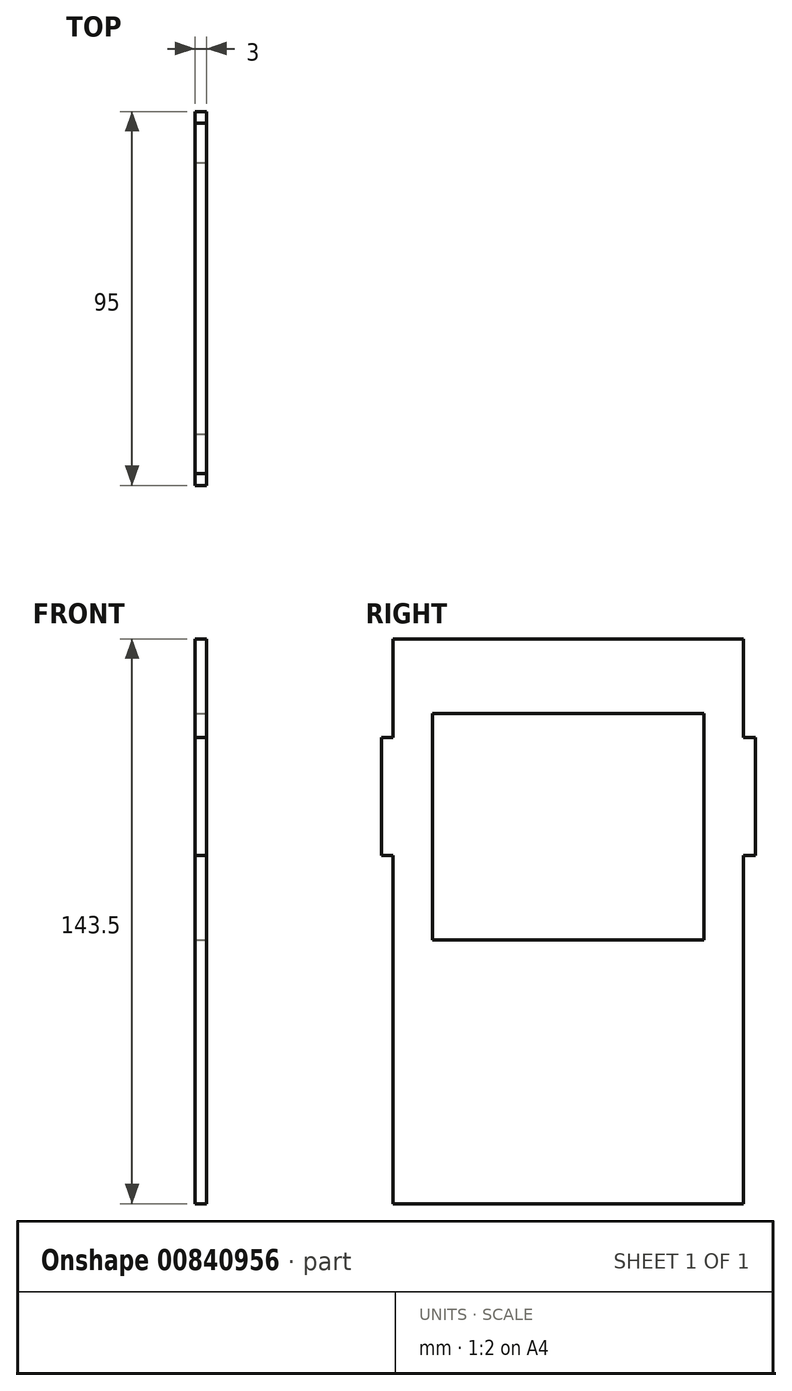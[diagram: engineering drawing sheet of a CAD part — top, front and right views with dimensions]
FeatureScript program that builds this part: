
annotation { "Feature Type Name" : "Feature", "Feature Type Description" : "" }
export const myFeature = defineFeature(function(context is Context, id is Id, definition is map)
    precondition{}
    {
        {
            var Q0;
            Q0=qCreatedBy(makeId("Right.planeOp"),FACE);
            var sketch = newSketch(context, id + "F0", { "sketchPlane" : qUnion([Q0])});
            skLineSegment(sketch, "E0.left", {"start": v(0, 0) * mm, "end": v(0, 143.5) * mm});
            skLineSegment(sketch, "E1.MirrorCS", {"start": v(0, 143.5) * mm, "end": v(-89, 143.5) * mm});
            skLineSegment(sketch, "E2", {"start": v(-89, 143.5) * mm, "end": v(-89, 0) * mm});
            skLineSegment(sketch, "E3", {"start": v(-89, 0) * mm, "end": v(0, 0) * mm});
            skLineSegment(sketch, "E4.bottom", {"start": v(0, 118.5) * mm, "end": v(3, 118.5) * mm});
            skLineSegment(sketch, "E4.top", {"start": v(0, 88.5) * mm, "end": v(3, 88.5) * mm});
            skLineSegment(sketch, "E4.left", {"start": v(0, 118.5) * mm, "end": v(0, 88.5) * mm});
            skLineSegment(sketch, "E4.right", {"start": v(3, 118.5) * mm, "end": v(3, 88.5) * mm});
            skLineSegment(sketch, "E5", {"start": v(-44.5, 143.5) * mm, "end": v(-44.5, 106.25) * mm, "construction": true});
            skLineSegment(sketch, "E6.MirrorCS", {"start": v(-89, 118.5) * mm, "end": v(-92, 118.5) * mm});
            skLineSegment(sketch, "E7.MirrorCS", {"start": v(-89, 88.5) * mm, "end": v(-92, 88.5) * mm});
            skLineSegment(sketch, "E8.MirrorCS", {"start": v(-92, 118.5) * mm, "end": v(-92, 88.5) * mm});
            skLineSegment(sketch, "E9.MirrorCS", {"start": v(-89, 118.5) * mm, "end": v(-89, 88.5) * mm});
            skSolve(sketch);
        }
        {
            var Q0;
            Q0 = qSketchRegion(id + "F0", true);
            extrude(context, id + "F1", {"entities" : qUnion([Q0]), "depth" : 3 * mm, "offsetDistance" : 25 * mm});
        }
        {
            var Q0;
            Q0=makeQuery(id+"F1.opExtrude","CAP_FACE",FACE,{"disambiguationData":[OSD([sQuery(id+"F0.wireOp",EDGE,"E0.left"),sQuery(id+"F0.wireOp",EDGE,"E1.MirrorCS"),sQuery(id+"F0.wireOp",EDGE,"59219e6d-5d3a-45a4-b07f-9ef35e72890b0.MirrorCS"),sQuery(id+"F0.wireOp",EDGE,"5a284621-8b43-45d7-a5f3-870bb1ad2ff50.MirrorCS"),sQuery(id+"F0.wireOp",EDGE,"e7b33866-3d08-4462-9678-68e19b66ad020.MirrorCS"),sQuery(id+"F0.wireOp",EDGE,"edf43a27-acfc-4a1f-a411-40ba9d5d53180.MirrorCS")])],"isStart":false});
            var sketch = newSketch(context, id + "F2", { "sketchPlane" : qUnion([Q0])});
            skLineSegment(sketch, "E10.bottom", {"start": v(-79, 124.5) * mm, "end": v(-10, 124.5) * mm});
            skLineSegment(sketch, "E10.top", {"start": v(-79, 67) * mm, "end": v(-10, 67) * mm});
            skLineSegment(sketch, "E10.left", {"start": v(-79, 124.5) * mm, "end": v(-79, 67) * mm});
            skLineSegment(sketch, "E10.right", {"start": v(-10, 124.5) * mm, "end": v(-10, 67) * mm});
            skSolve(sketch);
        }
        {
            var Q0;
            Q0 = qSketchRegion(id + "F2", true);
            extrude(context, id + "F3", {"entities" : qUnion([Q0]), "operationType" : NewBodyOperationType.REMOVE, "oppositeDirection" : true, "depth" : 25 * mm, "offsetDistance" : 25 * mm});
        }
    });
